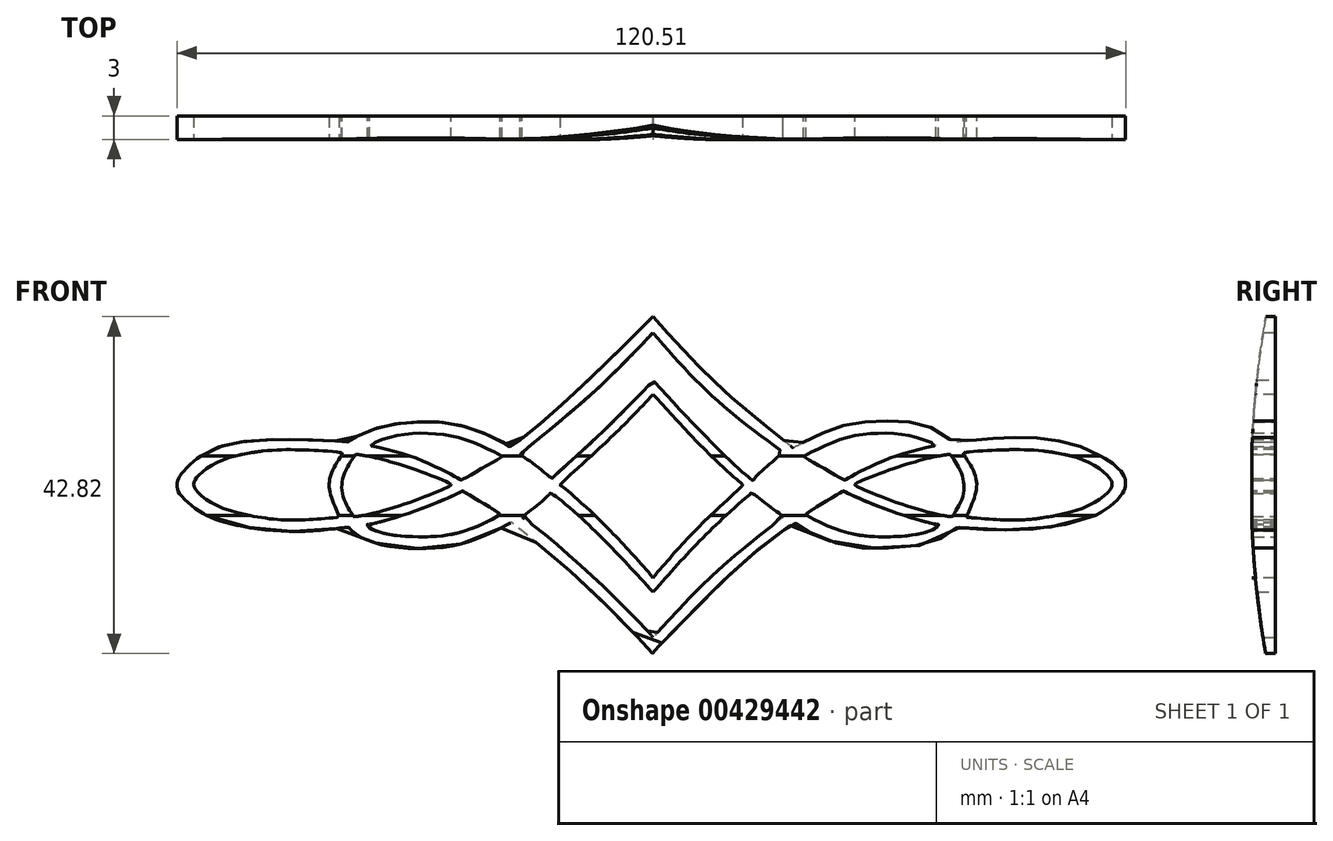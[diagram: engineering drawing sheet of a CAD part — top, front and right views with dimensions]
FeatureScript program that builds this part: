
annotation { "Feature Type Name" : "Feature", "Feature Type Description" : "" }
export const myFeature = defineFeature(function(context is Context, id is Id, definition is map)
    precondition{}
    {
        {
            var Q0;
            Q0=qCreatedBy(makeId("Front.planeOp"),FACE);
            var sketch = newSketch(context, id + "F0", { "sketchPlane" : qUnion([Q0])});
            skFitSpline(sketch, "E0", {"points": [v(19.17, 13.64) * mm, v(22.92, 15.4) * mm, v(27.21, 16.45) * mm, v(33.16, 16.12) * mm, v(35.97, 15.02) * mm, v(35.95, 15) * mm, v(30.5, 13.54) * mm, v(24.37, 10.6) * mm, v(24.32, 10.6) * mm, v(19.2, 13.58) * mm, v(19.17, 13.64) * mm]});
            skFitSpline(sketch, "E1", {"points": [v(19.48, 6.32) * mm, v(24.1, 9.17) * mm, v(24.2, 9.2) * mm, v(28.55, 7.3) * mm, v(36.11, 5) * mm, v(36.27, 5) * mm, v(36.2, 4.76) * mm, v(34, 3.8) * mm, v(27.38, 3.47) * mm, v(22.6, 4.6) * mm, v(19.47, 6.2) * mm, v(19.48, 6.32) * mm]});
            skFitSpline(sketch, "E2", {"points": [v(25.65, 10.05) * mm, v(30.04, 11.88) * mm, v(35.8, 13.55) * mm, v(37.64, 13.88) * mm, v(37.74, 13.85) * mm, v(39.07, 11.74) * mm, v(39.28, 8.29) * mm, v(38.08, 6.04) * mm, v(38.02, 5.96) * mm, v(32.47, 7.25) * mm, v(25.7, 9.94) * mm, v(25.65, 10.05) * mm]});
            skFitSpline(sketch, "E3", {"points": [v(39.54, 14.06) * mm, v(44.76, 14.45) * mm, v(50.18, 14.21) * mm, v(55.44, 12.81) * mm, v(57.97, 10.9) * mm, v(58.32, 10.24) * mm, v(58.12, 9.46) * mm, v(55.28, 7.32) * mm, v(49.9, 5.88) * mm, v(45.35, 5.53) * mm, v(39.9, 5.88) * mm, v(39.85, 5.9) * mm, v(40.76, 8.19) * mm, v(40.88, 11.38) * mm, v(39.49, 13.92) * mm, v(39.54, 14.06) * mm]});
            skFitSpline(sketch, "E4.MirrorC", {"points": [v(-19.17, 13.64) * mm, v(-22.91, 15.4) * mm, v(-27.21, 16.45) * mm, v(-33.16, 16.12) * mm, v(-35.97, 15.02) * mm, v(-35.95, 15) * mm, v(-30.5, 13.53) * mm, v(-24.37, 10.6) * mm, v(-24.32, 10.6) * mm, v(-19.2, 13.57) * mm, v(-19.17, 13.64) * mm]});
            skFitSpline(sketch, "E5.MirrorC", {"points": [v(-25.65, 10.04) * mm, v(-30.04, 11.88) * mm, v(-35.8, 13.55) * mm, v(-37.63, 13.88) * mm, v(-37.74, 13.85) * mm, v(-39.06, 11.74) * mm, v(-39.28, 8.28) * mm, v(-38.08, 6.04) * mm, v(-38.02, 5.96) * mm, v(-32.47, 7.24) * mm, v(-25.7, 9.94) * mm, v(-25.65, 10.04) * mm]});
            skFitSpline(sketch, "E6.MirrorC", {"points": [v(-19.48, 6.32) * mm, v(-24.1, 9.17) * mm, v(-24.19, 9.2) * mm, v(-28.55, 7.29) * mm, v(-36.1, 4.99) * mm, v(-36.26, 4.99) * mm, v(-36.2, 4.76) * mm, v(-34, 3.8) * mm, v(-27.38, 3.47) * mm, v(-22.6, 4.6) * mm, v(-19.46, 6.2) * mm, v(-19.48, 6.32) * mm]});
            skFitSpline(sketch, "E7.MirrorC", {"points": [v(-39.54, 14.05) * mm, v(-44.76, 14.44) * mm, v(-50.18, 14.2) * mm, v(-55.43, 12.8) * mm, v(-57.97, 10.9) * mm, v(-58.32, 10.23) * mm, v(-58.12, 9.46) * mm, v(-55.28, 7.31) * mm, v(-49.9, 5.87) * mm, v(-45.34, 5.52) * mm, v(-39.9, 5.87) * mm, v(-39.84, 5.9) * mm, v(-40.76, 8.18) * mm, v(-40.88, 11.38) * mm, v(-39.48, 13.92) * mm, v(-39.54, 14.05) * mm]});
            skFitSpline(sketch, "E8", {"points": [v(0, 31.37) * mm, v(8.23, 22.72) * mm, v(17.73, 14.73) * mm, v(17.75, 14.71) * mm, v(22.99, 17.15) * mm, v(29.07, 18.08) * mm, v(35.16, 17.35) * mm, v(38.04, 15.48) * mm, v(38.09, 15.41) * mm, v(48.03, 16.02) * mm, v(57.43, 13.35) * mm, v(59.74, 11.3) * mm, v(60.04, 10.32) * mm, v(59.84, 9.24) * mm, v(56.15, 6.08) * mm, v(46.84, 4.33) * mm, v(41.4, 4.34) * mm, v(38.83, 4.64) * mm, v(38.68, 4.65) * mm, v(36.58, 3.15) * mm, v(29.74, 1.98) * mm, v(23.04, 2.67) * mm, v(18.14, 5.06) * mm, v(18.03, 5.15) * mm, v(12.7, 1.23) * mm, v(3.37, -7.78) * mm, v(0, -11.4) * mm, v(0, -11.45) * mm, v(-8.22, -3.06) * mm, v(-17.87, 5.18) * mm, v(-17.95, 5.23) * mm, v(-21.88, 3.31) * mm, v(-29.76, 1.89) * mm, v(-36.83, 3.2) * mm, v(-38.52, 4.49) * mm, v(-38.62, 4.59) * mm, v(-43.8, 4.1) * mm, v(-53.37, 4.96) * mm, v(-57.48, 6.57) * mm, v(-60.23, 9.06) * mm, v(-60.45, 10.07) * mm, v(-60.09, 11.1) * mm, v(-57.34, 13.71) * mm, v(-50.42, 15.64) * mm, v(-39.04, 15.45) * mm, v(-38.85, 15.45) * mm, v(-36.22, 16.81) * mm, v(-29.9, 17.99) * mm, v(-23.12, 17.17) * mm, v(-18.42, 14.99) * mm, v(-18.2, 14.86) * mm, v(-13.69, 18.33) * mm, v(-4.68, 26.71) * mm, v(0, 31.36) * mm, v(0, 31.37) * mm]});
            skFitSpline(sketch, "E9", {"points": [v(-0.02, 29.32) * mm, v(7.55, 21.27) * mm, v(16.4, 14.2) * mm, v(16.4, 14.07) * mm, v(14.5, 12.35) * mm, v(12.84, 10.7) * mm, v(12.76, 10.56) * mm, v(5.71, 17.13) * mm, v(0, 23.29) * mm, v(0, 23.28) * mm, v(-6.75, 16.4) * mm, v(-12.7, 10.9) * mm, v(-12.8, 10.83) * mm, v(-15.02, 12.55) * mm, v(-16.8, 13.73) * mm, v(-16.9, 13.77) * mm, v(-7.66, 21.67) * mm, v(-0.03, 29.31) * mm, v(-0.02, 29.32) * mm]});
            skFitSpline(sketch, "E10", {"points": [v(0, 21.5) * mm, v(5.04, 16.04) * mm, v(11.26, 10.14) * mm, v(11.37, 9.98) * mm, v(5.81, 4.63) * mm, v(0, -1.81) * mm, v(0, -1.8) * mm, v(-5.78, 4.53) * mm, v(-11.72, 9.93) * mm, v(-11.78, 9.99) * mm, v(-5.84, 15.53) * mm, v(-0.02, 21.47) * mm, v(0, 21.5) * mm]});
            skFitSpline(sketch, "E11", {"points": [v(0, -3.62) * mm, v(6.17, 3.1) * mm, v(12.42, 8.88) * mm, v(12.56, 8.94) * mm, v(14.38, 7.59) * mm, v(16.47, 6.05) * mm, v(16.5, 5.94) * mm, v(8.56, -0.6) * mm, v(0, -9.4) * mm, v(0, -9.4) * mm, v(-8, -1.34) * mm, v(-16.58, 5.84) * mm, v(-16.63, 5.87) * mm, v(-14.6, 7.49) * mm, v(-13.13, 8.83) * mm, v(-13.02, 8.92) * mm, v(-6.88, 3.67) * mm, v(-0.02, -3.62) * mm, v(0, -3.62) * mm]});
            skLineSegment(sketch, "E12", {"start": v(-60.45, 10.07) * mm, "end": v(60.04, 10.32) * mm, "construction": true});
            skSolve(sketch);
        }
        {
            var Q0;
            Q0=makeQuery(id+"F0.imprint","IMPRINT",FACE,{"disambiguationData":[TD([[makeQuery(id+"F0.imprint","IMPRINT",EDGE,{"derivedFrom":sQuery(id+"F0.wireOp",EDGE,"E0")}),1.0]])]});
            extrude(context, id + "F1", {"entities" : qUnion([Q0]), "depth" : 3 * mm});
        }
        {
            var Q0;
            Q0=qCreatedBy(makeId("Right.planeOp"),FACE);
            var sketch = newSketch(context, id + "F2", { "sketchPlane" : qUnion([Q0])});
            skArc(sketch, "E13", {"start": v(0, 37.33) * mm, "mid": v(-3.06, 9.9) * mm, "end": v(0, -17.55) * mm});
            skLineSegment(sketch, "E14", {"start": v(0, 37.33) * mm, "end": v(-8.52, 37.33) * mm});
            skLineSegment(sketch, "E15", {"start": v(-8.52, 37.33) * mm, "end": v(-8.52, -17.22) * mm});
            skLineSegment(sketch, "E16", {"start": v(-8.52, -17.22) * mm, "end": v(0, -17.55) * mm});
            skSolve(sketch);
        }
        {
            var Q0;
            Q0 = qSketchRegion(id + "F2", true);
            extrude(context, id + "F3", {"entities" : qUnion([Q0]), "operationType" : NewBodyOperationType.REMOVE, "endBound" : BoundingType.SYMMETRIC, "depth" : 130 * mm});
        }
    });
